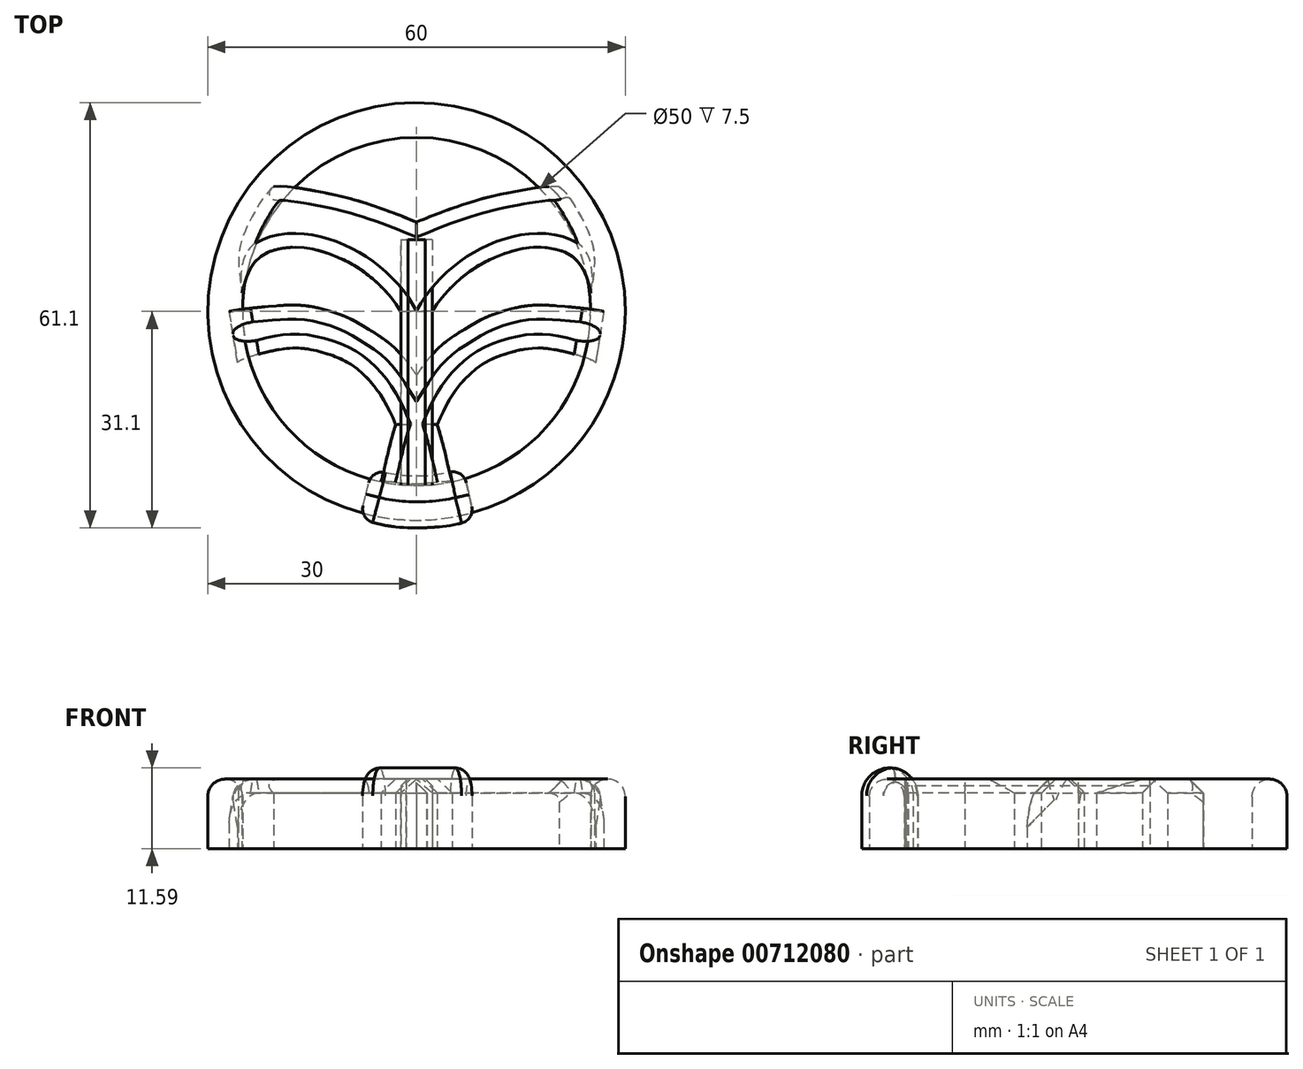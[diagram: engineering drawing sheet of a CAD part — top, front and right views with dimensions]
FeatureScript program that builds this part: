
annotation { "Feature Type Name" : "Feature", "Feature Type Description" : "" }
export const myFeature = defineFeature(function(context is Context, id is Id, definition is map)
    precondition{}
    {
        {
            var Q0;
            Q0=qCreatedBy(makeId("Top.planeOp"),FACE);
            var sketch = newSketch(context, id + "F0", { "sketchPlane" : qUnion([Q0])});
            skCircle(sketch, "E0", {"center": v(0, 0) * mm, "radius": 30 * mm});
            skCircle(sketch, "E1", {"center": v(0, 0) * mm, "radius": 25 * mm});
            skFitSpline(sketch, "E2", {"points": [v(-19.4, 4.73) * mm, v(-15.74, 4.78) * mm, v(-12.2, 3.75) * mm, v(-8.7, 1.73) * mm, v(-7.51, 0.63) * mm, v(-6.82, 0) * mm, v(-7.18, 4.3) * mm, v(-10.74, 8.15) * mm, v(-15.08, 10.06) * mm, v(-17.82, 9.82) * mm, v(-19.9, 6.08) * mm, v(-19.4, 4.73) * mm]});
            skFitSpline(sketch, "E3", {"points": [v(-17.31, 18.03) * mm, v(-13.45, 16.3) * mm, v(-7.69, 14.97) * mm, v(-1.64, 14.41) * mm, v(2.1, 14.39) * mm, v(8.43, 14.83) * mm, v(18.52, 16.8) * mm], "startDerivative": vector(25.83, -13.04) * mm, "endDerivative": vector(47.8, 10.6) * mm});
            skLineSegment(sketch, "E4", {"start": v(0, 25) * mm, "end": v(0, -25) * mm});
            skFitSpline(sketch, "E5.MirrorC", {"points": [v(19.4, 4.73) * mm, v(15.74, 4.78) * mm, v(12.2, 3.75) * mm, v(8.7, 1.73) * mm, v(7.51, 0.63) * mm, v(6.82, 0) * mm, v(7.18, 4.3) * mm, v(10.74, 8.15) * mm, v(15.08, 10.06) * mm, v(17.82, 9.82) * mm, v(19.9, 6.08) * mm, v(19.4, 4.73) * mm]});
            skEllipse(sketch, "E6", {"center": v(-15.1, -7.92) * mm, "majorRadius": 10.38 * mm, "minorRadius": 6.65 * mm, "majorAxis": v(-0.47, 0.88)});
            skSolve(sketch);
        }
        {
            var Q0;
            Q0=makeQuery(id+"F0.imprint","IMPRINT",FACE,{"disambiguationData":[TD([[makeQuery(id+"F0.imprint","IMPRINT",EDGE,{"derivedFrom":sQuery(id+"F0.wireOp",EDGE,"imP7k3WO-HDCw-tjEA-zSIR-fysF2QLLcROs")}),-1.0]])]});
            var Q1;
            Q1=makeQuery(id+"F0.imprint","IMPRINT",FACE,{"disambiguationData":[TD([[makeQuery(id+"F0.imprint","IMPRINT",EDGE,{"derivedFrom":sQuery(id+"F0.wireOp",EDGE,"E0")}),1.0]])]});
            extrude(context, id + "F1", {"entities" : qUnion([Q0, Q1]), "depth" : 10 * mm, "offsetDistance" : 25 * mm});
        }
        {
            var Q0;
            Q0=makeQuery(id+"F1.opExtrude","CAP_EDGE",EDGE,{"disambiguationData":[OSD([sQuery(id+"F0.wireOp",EDGE,"E1")])],"isStart":false});
            var Q1;
            Q1=makeQuery(id+"F1.opExtrude","CAP_EDGE",EDGE,{"disambiguationData":[OSD([sQuery(id+"F0.wireOp",EDGE,"E0")])],"isStart":false});
            fillet(context, id + "F2", {"entities" : qUnion([Q0, Q1]), "radius" : 2.5 * mm, "tangentPropagation" : true, "allowEdgeOverflow" : false});
        }
        {
            var Q0;
            Q0=qCreatedBy(makeId("Top.planeOp"),FACE);
            var sketch = newSketch(context, id + "F3", { "sketchPlane" : qUnion([Q0])});
            skFitSpline(sketch, "E7", {"points": [v(1.48, -24.88) * mm, v(1.43, -22.94) * mm, v(1.7, -20.78) * mm, v(2.24, -18.4) * mm, v(3.53, -15.01) * mm, v(4.93, -12.37) * mm, v(6.71, -10) * mm, v(9.68, -7.46) * mm, v(13.13, -6) * mm, v(17.34, -5.25) * mm, v(22.35, -6.06) * mm, v(25.74, -7.32) * mm], "startDerivative": vector(-1.75, 26.61) * mm, "endDerivative": vector(17.9, -14.55) * mm});
            skFitSpline(sketch, "E8", {"points": [v(26.9, 0) * mm, v(20.9, 0.75) * mm, v(17.01, 0.9) * mm, v(13.72, 0.4) * mm, v(10.1, -0.8) * mm, v(7.27, -2.35) * mm, v(2.99, -5.42) * mm, v(-0.82, -10.58) * mm, v(-1.9, -13.14) * mm, v(-3.5, -17.94) * mm, v(-4.87, -23.63) * mm, v(-5.11, -24.4) * mm], "startDerivative": vector(-42.42, 9.25) * mm, "endDerivative": vector(-5.23, -13.09) * mm});
            skLineSegment(sketch, "E9", {"start": v(26.9, 0) * mm, "end": v(25.74, -7.32) * mm});
            skLineSegment(sketch, "E10", {"start": v(-5.11, -24.4) * mm, "end": v(1.48, -24.88) * mm});
            skFitSpline(sketch, "E11.MirrorCS", {"points": [v(-26.9, 0) * mm, v(-20.9, 0.75) * mm, v(-17.01, 0.9) * mm, v(-13.72, 0.4) * mm, v(-10.1, -0.8) * mm, v(-7.27, -2.35) * mm, v(-2.99, -5.42) * mm, v(0.82, -10.58) * mm, v(1.9, -13.14) * mm, v(3.5, -17.94) * mm, v(4.87, -23.63) * mm, v(5.11, -24.4) * mm], "startDerivative": vector(42.42, 9.25) * mm, "endDerivative": vector(5.23, -13.09) * mm});
            skFitSpline(sketch, "E12.MirrorCS", {"points": [v(-1.48, -24.88) * mm, v(-1.43, -22.94) * mm, v(-1.7, -20.78) * mm, v(-2.24, -18.4) * mm, v(-3.53, -15.01) * mm, v(-4.93, -12.37) * mm, v(-6.71, -10) * mm, v(-9.68, -7.46) * mm, v(-13.13, -6) * mm, v(-17.34, -5.25) * mm, v(-22.35, -6.06) * mm, v(-25.74, -7.32) * mm], "startDerivative": vector(1.75, 26.61) * mm, "endDerivative": vector(-17.9, -14.55) * mm});
            skLineSegment(sketch, "E13.MirrorCS", {"start": v(5.11, -24.4) * mm, "end": v(-1.48, -24.88) * mm});
            skLineSegment(sketch, "E14.MirrorCS", {"start": v(-26.9, 0) * mm, "end": v(-25.74, -7.32) * mm});
            skSolve(sketch);
        }
        {
            var Q0;
            Q0 = qSketchRegion(id + "F3", true);
            extrude(context, id + "F4", {"entities" : qUnion([Q0]), "depth" : 10 * mm, "offsetDistance" : 25 * mm});
        }
        {
            var Q0;
            Q0=makeQuery(id+"F4.opExtrude","CAP_EDGE",EDGE,{"disambiguationData":[OSD([sQuery(id+"F3.wireOp",EDGE,"E7")])],"isStart":false});
            var Q1;
            Q1=makeQuery(id+"F4.opExtrude","CAP_EDGE",EDGE,{"disambiguationData":[OSD([sQuery(id+"F3.wireOp",EDGE,"E8")])],"isStart":false});
            var Q2;
            {var subQ0=sQuery(id+"F3.wireOp",EDGE,"E11.MirrorCS");Q2=makeQuery(id+"F4.opExtrude","CAP_EDGE",EDGE,{"disambiguationData":[OSD([subQ0]),TDD([makeQuery(id+"F3.imprint","IMPRINT",EDGE,{"disambiguationData":[TD([[makeQuery(id+"F3.imprint","INTERSECT",VERTEX,{"derivedFrom":[subQ0,sQuery(id+"F3.wireOp",EDGE,"E14.MirrorCS")]}),-1.0]])],"derivedFrom":subQ0})])],"isStart":false});}
            var Q3;
            {var subQ0=sQuery(id+"F3.wireOp",EDGE,"E12.MirrorCS");Q3=makeQuery(id+"F4.opExtrude","CAP_EDGE",EDGE,{"disambiguationData":[OSD([subQ0]),TDD([makeQuery(id+"F3.imprint","IMPRINT",EDGE,{"disambiguationData":[TD([[makeQuery(id+"F3.imprint","INTERSECT",VERTEX,{"derivedFrom":[subQ0,sQuery(id+"F3.wireOp",EDGE,"E14.MirrorCS")]}),1.0]])],"derivedFrom":subQ0})])],"isStart":false});}
            var Q4;
            {var subQ0=sQuery(id+"F3.wireOp",EDGE,"E11.MirrorCS");Q4=makeQuery(id+"F4.opExtrude","CAP_EDGE",EDGE,{"disambiguationData":[OSD([subQ0]),TDD([makeQuery(id+"F3.imprint","IMPRINT",EDGE,{"disambiguationData":[TD([[makeQuery(id+"F3.imprint","INTERSECT",VERTEX,{"derivedFrom":[subQ0,sQuery(id+"F3.wireOp",EDGE,"E13.MirrorCS")]}),1.0]])],"derivedFrom":subQ0})])],"isStart":false});}
            chamfer(context, id + "F5", {"entities" : qUnion([Q0, Q1, Q2, Q3, Q4]), "width" : 2 * mm, "tangentPropagation" : true});
        }
        {
            var Q0;
            Q0=qCreatedBy(makeId("Top.planeOp"),FACE);
            var sketch = newSketch(context, id + "F6", { "sketchPlane" : qUnion([Q0])});
            skLineSegment(sketch, "E15", {"start": v(2.25, 0) * mm, "end": v(2.25, -24.9) * mm});
            skLineSegment(sketch, "E16", {"start": v(2.25, -24.9) * mm, "end": v(-2.23, -24.9) * mm});
            skLineSegment(sketch, "E17", {"start": v(-2.23, -24.9) * mm, "end": v(-2.23, 0) * mm});
            skLineSegment(sketch, "E18", {"start": v(2.25, 0) * mm, "end": v(2.25, 10.33) * mm});
            skLineSegment(sketch, "E19", {"start": v(2.25, 10.33) * mm, "end": v(-2.23, 10.33) * mm});
            skLineSegment(sketch, "E20", {"start": v(-2.23, 10.33) * mm, "end": v(-2.23, 0) * mm});
            skSolve(sketch);
        }
        {
            var Q0;
            Q0=makeQuery(id+"F6.imprint","IMPRINT",FACE,{"disambiguationData":[TD([[makeQuery(id+"F6.imprint","IMPRINT",EDGE,{"derivedFrom":sQuery(id+"F6.wireOp",EDGE,"E15")}),-1.0]])]});
            extrude(context, id + "F7", {"entities" : qUnion([Q0]), "depth" : 10 * mm, "offsetDistance" : 25 * mm});
        }
        {
            var Q0;
            Q0=makeQuery(id+"F7.opExtrude","CAP_EDGE",EDGE,{"disambiguationData":[OSD([sQuery(id+"F6.wireOp",EDGE,"E17")])],"isStart":false});
            var Q1;
            Q1=makeQuery(id+"F7.opExtrude","CAP_EDGE",EDGE,{"disambiguationData":[OSD([sQuery(id+"F6.wireOp",EDGE,"E15")])],"isStart":false});
            chamfer(context, id + "F8", {"entities" : qUnion([Q0, Q1]), "width" : 1 * mm, "tangentPropagation" : true});
        }
        {
            var Q0;
            Q0=qCreatedBy(makeId("Top.planeOp"),FACE);
            var sketch = newSketch(context, id + "F9", { "sketchPlane" : qUnion([Q0])});
            skFitSpline(sketch, "E21", {"points": [v(2.28, 0) * mm, v(4.82, 3.3) * mm, v(9.01, 6.64) * mm, v(13.63, 8.63) * mm, v(17.6, 9.21) * mm, v(22.15, 8.08) * mm, v(24.38, 5.07) * mm, v(25.16, 1.49) * mm, v(24.97, 0) * mm], "startDerivative": vector(15.98, 27.15) * mm, "endDerivative": vector(0.32, -16.22) * mm});
            skFitSpline(sketch, "E22", {"points": [v(0, 12.83) * mm, v(3.41, 14.19) * mm, v(8.77, 16) * mm, v(13.4, 17.09) * mm, v(20.51, 17.95) * mm], "startDerivative": vector(14.36, 5.96) * mm, "endDerivative": vector(19.32, -1.45) * mm});
            skFitSpline(sketch, "E23", {"points": [v(20.51, 17.95) * mm, v(23.23, 14.3) * mm, v(25.48, 8.52) * mm, v(25.07, 2.62) * mm, v(24.97, 0.42) * mm], "startDerivative": vector(12.85, -10.8) * mm, "endDerivative": vector(0.5, -10.65) * mm});
            skLineSegment(sketch, "E24", {"start": v(0, 12.83) * mm, "end": v(0, 0) * mm});
            skLineSegment(sketch, "E25", {"start": v(0, 0) * mm, "end": v(2.28, 0) * mm});
            skFitSpline(sketch, "E26.MirrorCS", {"points": [v(0, 12.83) * mm, v(-3.41, 14.19) * mm, v(-8.77, 16) * mm, v(-13.4, 17.09) * mm, v(-20.51, 17.95) * mm], "startDerivative": vector(-14.36, 5.96) * mm, "endDerivative": vector(-19.32, -1.45) * mm});
            skFitSpline(sketch, "E27.MirrorCS", {"points": [v(-2.28, 0) * mm, v(-4.82, 3.3) * mm, v(-9.01, 6.64) * mm, v(-13.63, 8.63) * mm, v(-17.6, 9.21) * mm, v(-22.15, 8.08) * mm, v(-24.38, 5.07) * mm, v(-25.16, 1.49) * mm, v(-24.97, 0) * mm], "startDerivative": vector(-15.98, 27.15) * mm, "endDerivative": vector(-0.32, -16.22) * mm});
            skLineSegment(sketch, "E28.MirrorCS", {"start": v(0, 0) * mm, "end": v(-2.28, 0) * mm});
            skFitSpline(sketch, "E29.MirrorCS", {"points": [v(-20.51, 17.95) * mm, v(-23.23, 14.3) * mm, v(-25.48, 8.52) * mm, v(-25.07, 2.62) * mm, v(-24.97, 0.42) * mm], "startDerivative": vector(-12.85, -10.8) * mm, "endDerivative": vector(-0.5, -10.65) * mm});
            skSolve(sketch);
        }
        {
            var Q0;
            {var subQ1=sQuery(id+"F9.wireOp",EDGE,"E22");Q0=makeQuery(id+"F9.imprint","IMPRINT",FACE,{"disambiguationData":[TD([[makeQuery(id+"F9.imprint","IMPRINT",EDGE,{"derivedFrom":subQ1}),-1.0]])]});}
            var Q1;
            Q1=makeQuery(id+"F9.imprint","IMPRINT",FACE,{"disambiguationData":[TD([[makeQuery(id+"F9.imprint","IMPRINT",EDGE,{"derivedFrom":sQuery(id+"F9.wireOp",EDGE,"E24")}),-1.0]])]});
            extrude(context, id + "F10", {"entities" : qUnion([Q0, Q1]), "depth" : 10 * mm, "offsetDistance" : 25 * mm});
        }
        {
            var Q0;
            Q0=makeQuery(id+"F10.opExtrude","CAP_EDGE",EDGE,{"disambiguationData":[OSD([sQuery(id+"F9.wireOp",EDGE,"E22")])],"isStart":false});
            var Q1;
            Q1=makeQuery(id+"F10.opExtrude","CAP_EDGE",EDGE,{"disambiguationData":[OSD([sQuery(id+"F9.wireOp",EDGE,"E21")])],"isStart":false});
            var Q2;
            Q2=makeQuery(id+"F10.opExtrude","CAP_EDGE",EDGE,{"disambiguationData":[OSD([sQuery(id+"F9.wireOp",EDGE,"E27.MirrorCS")])],"isStart":false});
            var Q3;
            Q3=makeQuery(id+"F10.opExtrude","CAP_EDGE",EDGE,{"disambiguationData":[OSD([sQuery(id+"F9.wireOp",EDGE,"E26.MirrorCS")])],"isStart":false});
            chamfer(context, id + "F11", {"entities" : qUnion([Q0, Q1, Q2, Q3]), "width" : 2 * mm, "tangentPropagation" : true});
        }
        {
            var Q0;
            Q0=qCreatedBy(makeId("Top.planeOp"),FACE);
            var sketch = newSketch(context, id + "F12", { "sketchPlane" : qUnion([Q0])});
            skFitSpline(sketch, "E30", {"points": [v(-8.14, -29.73) * mm, v(-4.78, -30.68) * mm, v(0, -31.1) * mm, v(5.66, -30.6) * mm, v(8.33, -29.84) * mm], "startDerivative": vector(14.01, -4.6) * mm, "endDerivative": vector(11.54, 4) * mm});
            skFitSpline(sketch, "E31", {"points": [v(-6.34, -22.56) * mm, v(-4.45, -23.14) * mm, v(-1.49, -23.56) * mm, v(1.42, -23.59) * mm, v(4.12, -23.2) * mm, v(6.74, -22.66) * mm], "startDerivative": vector(10.42, -3.04) * mm, "endDerivative": vector(12.16, 3.35) * mm});
            skLineSegment(sketch, "E32", {"start": v(-8.14, -29.73) * mm, "end": v(-6.34, -22.56) * mm});
            skLineSegment(sketch, "E33", {"start": v(8.33, -29.84) * mm, "end": v(6.74, -22.66) * mm});
            skSolve(sketch);
        }
        {
            var Q0;
            Q0=makeQuery(id+"F12.imprint","IMPRINT",FACE,{"disambiguationData":[TD([[makeQuery(id+"F12.imprint","IMPRINT",EDGE,{"derivedFrom":sQuery(id+"F12.wireOp",EDGE,"E30")}),1.0]])]});
            extrude(context, id + "F13", {"entities" : qUnion([Q0]), "depth" : 11.6 * mm, "offsetDistance" : 25 * mm});
        }
        {
            var Q0;
            Q0=makeQuery(id+"F13.opExtrude","CAP_EDGE",EDGE,{"disambiguationData":[OSD([sQuery(id+"F12.wireOp",EDGE,"E31")])],"isStart":false});
            var Q1;
            Q1=makeQuery(id+"F13.opExtrude","CAP_EDGE",EDGE,{"disambiguationData":[OSD([sQuery(id+"F12.wireOp",EDGE,"E30")])],"isStart":false});
            fillet(context, id + "F14", {"entities" : qUnion([Q0, Q1]), "radius" : 4 * mm, "tangentPropagation" : true, "allowEdgeOverflow" : false});
        }
        {
            var Q0;
            Q0=makeQuery(id+"F14.opFillet","BLEND_EDGE",EDGE,{"blendedFrom":[makeQuery(id+"F13.opExtrude","CAP_EDGE",EDGE,{"disambiguationData":[OSD([sQuery(id+"F12.wireOp",EDGE,"E30")])],"isStart":false}),makeQuery(id+"F13.opExtrude","SWEPT_FACE",FACE,{"disambiguationData":[OSD([sQuery(id+"F12.wireOp",EDGE,"E33")])]})],"blendedInto":[makeQuery(id+"F13.opExtrude","SWEPT_FACE",FACE,{"disambiguationData":[OSD([sQuery(id+"F12.wireOp",EDGE,"E33")])]})]});
            var Q1;
            Q1=makeQuery(id+"F14.opFillet","BLEND_EDGE",EDGE,{"blendedFrom":[makeQuery(id+"F13.opExtrude","CAP_EDGE",EDGE,{"disambiguationData":[OSD([sQuery(id+"F12.wireOp",EDGE,"E31")])],"isStart":false}),makeQuery(id+"F13.opExtrude","SWEPT_FACE",FACE,{"disambiguationData":[OSD([sQuery(id+"F12.wireOp",EDGE,"E33")])]})],"blendedInto":[makeQuery(id+"F13.opExtrude","SWEPT_FACE",FACE,{"disambiguationData":[OSD([sQuery(id+"F12.wireOp",EDGE,"E33")])]})]});
            var Q2;
            Q2=makeQuery(id+"F14.opFillet","BLEND_EDGE",EDGE,{"blendedFrom":[makeQuery(id+"F13.opExtrude","CAP_EDGE",EDGE,{"disambiguationData":[OSD([sQuery(id+"F12.wireOp",EDGE,"E30")])],"isStart":false}),makeQuery(id+"F13.opExtrude","SWEPT_FACE",FACE,{"disambiguationData":[OSD([sQuery(id+"F12.wireOp",EDGE,"E32")])]})],"blendedInto":[makeQuery(id+"F13.opExtrude","SWEPT_FACE",FACE,{"disambiguationData":[OSD([sQuery(id+"F12.wireOp",EDGE,"E32")])]})]});
            var Q3;
            Q3=makeQuery(id+"F14.opFillet","BLEND_EDGE",EDGE,{"blendedFrom":[makeQuery(id+"F13.opExtrude","CAP_EDGE",EDGE,{"disambiguationData":[OSD([sQuery(id+"F12.wireOp",EDGE,"E31")])],"isStart":false}),makeQuery(id+"F13.opExtrude","SWEPT_FACE",FACE,{"disambiguationData":[OSD([sQuery(id+"F12.wireOp",EDGE,"E32")])]})],"blendedInto":[makeQuery(id+"F13.opExtrude","SWEPT_FACE",FACE,{"disambiguationData":[OSD([sQuery(id+"F12.wireOp",EDGE,"E32")])]})]});
            fillet(context, id + "F15", {"entities" : qUnion([Q0, Q1, Q2, Q3]), "radius" : 2 * mm, "tangentPropagation" : true, "allowEdgeOverflow" : false});
        }
        {
            var Q0;
            {var subQ0=sQuery(id+"F3.wireOp",EDGE,"E9");var subQ1=sQuery(id+"F3.wireOp",EDGE,"E8");Q0=makeQuery(id+"F5.opChamfer","BLEND_EDGE",EDGE,{"blendedFrom":[makeQuery(id+"F4.opExtrude","CAP_EDGE",EDGE,{"disambiguationData":[OSD([subQ1]),TDD([makeQuery(id+"F3.imprint","IMPRINT",EDGE,{"disambiguationData":[TD([[makeQuery(id+"F3.imprint","INTERSECT",VERTEX,{"derivedFrom":[subQ1,subQ0]}),-1.0]])],"derivedFrom":subQ1})])],"isStart":false}),makeQuery(id+"F4.opExtrude","SWEPT_FACE",FACE,{"disambiguationData":[OSD([subQ0])]})],"blendedInto":[makeQuery(id+"F4.opExtrude","SWEPT_FACE",FACE,{"disambiguationData":[OSD([subQ0])]})]});}
            var Q1;
            Q1=makeQuery(id+"F4.opExtrude","CAP_EDGE",EDGE,{"disambiguationData":[OSD([sQuery(id+"F3.wireOp",EDGE,"E9")])],"isStart":false});
            var Q2;
            {var subQ0=sQuery(id+"F3.wireOp",EDGE,"E9");var subQ1=sQuery(id+"F3.wireOp",EDGE,"E7");Q2=makeQuery(id+"F5.opChamfer","BLEND_EDGE",EDGE,{"blendedFrom":[makeQuery(id+"F4.opExtrude","CAP_EDGE",EDGE,{"disambiguationData":[OSD([subQ1]),TDD([makeQuery(id+"F3.imprint","IMPRINT",EDGE,{"disambiguationData":[TD([[makeQuery(id+"F3.imprint","INTERSECT",VERTEX,{"derivedFrom":[subQ1,subQ0]}),1.0]])],"derivedFrom":subQ1})])],"isStart":false}),makeQuery(id+"F4.opExtrude","SWEPT_FACE",FACE,{"disambiguationData":[OSD([subQ0])]})],"blendedInto":[makeQuery(id+"F4.opExtrude","SWEPT_FACE",FACE,{"disambiguationData":[OSD([subQ0])]})]});}
            fillet(context, id + "F16", {"entities" : qUnion([Q0, Q1, Q2]), "radius" : 3 * mm, "tangentPropagation" : true, "allowEdgeOverflow" : false});
        }
        {
            var Q0;
            {var subQ0=sQuery(id+"F3.wireOp",EDGE,"E14.MirrorCS");var subQ1=sQuery(id+"F3.wireOp",EDGE,"E12.MirrorCS");Q0=makeQuery(id+"F5.opChamfer","BLEND_EDGE",EDGE,{"blendedFrom":[makeQuery(id+"F4.opExtrude","CAP_EDGE",EDGE,{"disambiguationData":[OSD([subQ1]),TDD([makeQuery(id+"F3.imprint","IMPRINT",EDGE,{"disambiguationData":[TD([[makeQuery(id+"F3.imprint","INTERSECT",VERTEX,{"derivedFrom":[subQ1,subQ0]}),1.0]])],"derivedFrom":subQ1})])],"isStart":false}),makeQuery(id+"F4.opExtrude","SWEPT_FACE",FACE,{"disambiguationData":[OSD([subQ0])]})],"blendedInto":[makeQuery(id+"F4.opExtrude","SWEPT_FACE",FACE,{"disambiguationData":[OSD([subQ0])]})]});}
            var Q1;
            Q1=makeQuery(id+"F4.opExtrude","CAP_EDGE",EDGE,{"disambiguationData":[OSD([sQuery(id+"F3.wireOp",EDGE,"E14.MirrorCS")])],"isStart":false});
            var Q2;
            {var subQ0=sQuery(id+"F3.wireOp",EDGE,"E14.MirrorCS");var subQ1=sQuery(id+"F3.wireOp",EDGE,"E11.MirrorCS");Q2=makeQuery(id+"F5.opChamfer","BLEND_EDGE",EDGE,{"blendedFrom":[makeQuery(id+"F4.opExtrude","CAP_EDGE",EDGE,{"disambiguationData":[OSD([subQ1]),TDD([makeQuery(id+"F3.imprint","IMPRINT",EDGE,{"disambiguationData":[TD([[makeQuery(id+"F3.imprint","INTERSECT",VERTEX,{"derivedFrom":[subQ1,subQ0]}),-1.0]])],"derivedFrom":subQ1})])],"isStart":false}),makeQuery(id+"F4.opExtrude","SWEPT_FACE",FACE,{"disambiguationData":[OSD([subQ0])]})],"blendedInto":[makeQuery(id+"F4.opExtrude","SWEPT_FACE",FACE,{"disambiguationData":[OSD([subQ0])]})]});}
            fillet(context, id + "F17", {"entities" : qUnion([Q0, Q1, Q2]), "radius" : 3 * mm, "tangentPropagation" : true, "allowEdgeOverflow" : false});
        }
        {
            var Q0;
            Q0=makeQuery(id+"F11.opChamfer","BLEND_EDGE",EDGE,{"blendedFrom":[makeQuery(id+"F10.opExtrude","CAP_EDGE",EDGE,{"disambiguationData":[OSD([sQuery(id+"F9.wireOp",EDGE,"E22")])],"isStart":false}),makeQuery(id+"F10.opExtrude","SWEPT_FACE",FACE,{"disambiguationData":[OSD([sQuery(id+"F9.wireOp",EDGE,"E23")])]})],"blendedInto":[makeQuery(id+"F10.opExtrude","SWEPT_FACE",FACE,{"disambiguationData":[OSD([sQuery(id+"F9.wireOp",EDGE,"E23")])]})]});
            var Q1;
            Q1=makeQuery(id+"F10.opExtrude","CAP_EDGE",EDGE,{"disambiguationData":[OSD([sQuery(id+"F9.wireOp",EDGE,"E23")])],"isStart":false});
            var Q2;
            Q2=makeQuery(id+"F10.opExtrude","CAP_EDGE",EDGE,{"disambiguationData":[OSD([sQuery(id+"F9.wireOp",EDGE,"E29.MirrorCS")])],"isStart":false});
            fillet(context, id + "F18", {"entities" : qUnion([Q0, Q1, Q2]), "radius" : 2 * mm, "tangentPropagation" : true, "allowEdgeOverflow" : false});
        }
    });
